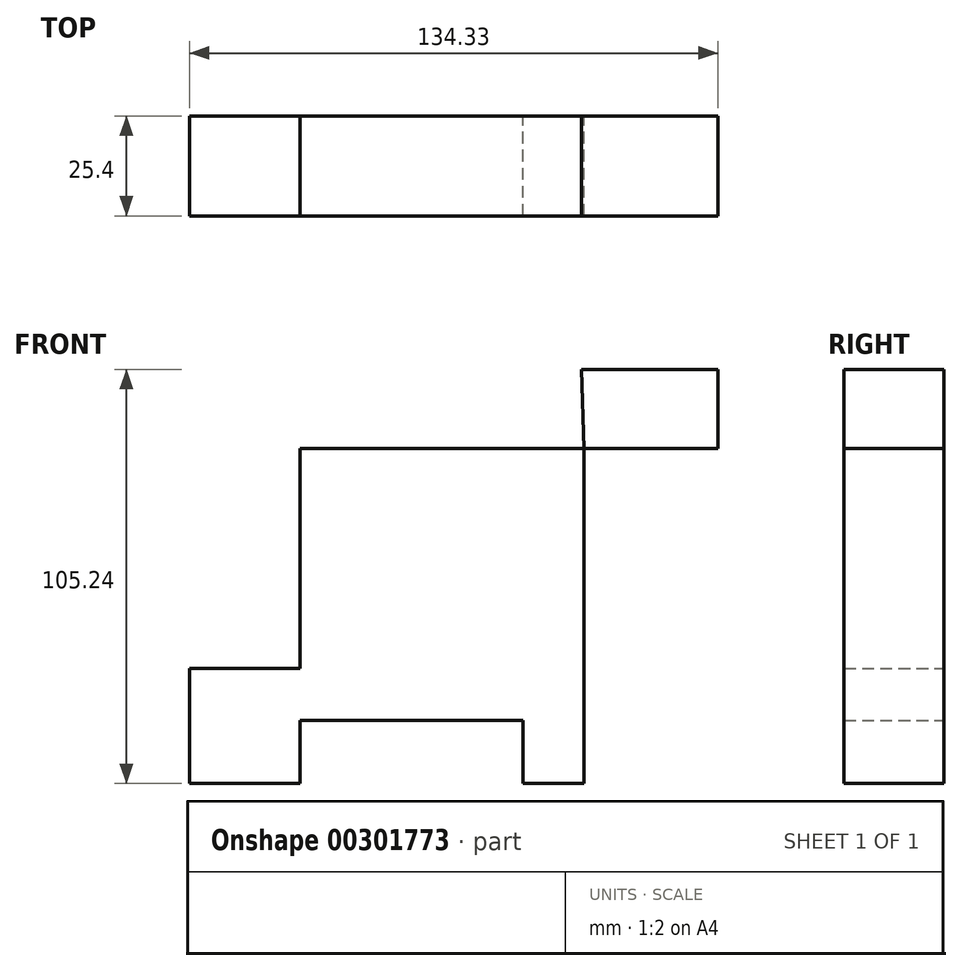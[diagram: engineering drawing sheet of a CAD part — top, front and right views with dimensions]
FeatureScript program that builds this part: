
annotation { "Feature Type Name" : "Feature", "Feature Type Description" : "" }
export const myFeature = defineFeature(function(context is Context, id is Id, definition is map)
    precondition{}
    {
        {
            var Q0;
            Q0=qCreatedBy(makeId("Front.planeOp"),FACE);
            var sketch = newSketch(context, id + "F0", { "sketchPlane" : qUnion([Q0])});
            skLineSegment(sketch, "E0", {"start": v(0, 55.87) * mm, "end": v(35.6, 55.87) * mm});
            skLineSegment(sketch, "E1", {"start": v(0, 55.87) * mm, "end": v(-36.52, 55.87) * mm});
            skLineSegment(sketch, "E2", {"start": v(-36.52, 55.87) * mm, "end": v(-36.52, 0) * mm});
            skLineSegment(sketch, "E3", {"start": v(-36.52, 0) * mm, "end": v(-64.69, 0) * mm});
            skLineSegment(sketch, "E4", {"start": v(-64.69, 0) * mm, "end": v(-64.69, -29.25) * mm});
            skLineSegment(sketch, "E5", {"start": v(-64.69, -29.25) * mm, "end": v(-36.52, -29.25) * mm});
            skLineSegment(sketch, "E6", {"start": v(-36.52, -29.25) * mm, "end": v(-36.52, -13.15) * mm});
            skLineSegment(sketch, "E7", {"start": v(35.6, 55.87) * mm, "end": v(35.6, -29.25) * mm});
            skLineSegment(sketch, "E8", {"start": v(35.6, -29.25) * mm, "end": v(20.12, -29.25) * mm});
            skLineSegment(sketch, "E9", {"start": v(20.12, -29.25) * mm, "end": v(20.12, -13.15) * mm});
            skLineSegment(sketch, "E10", {"start": v(-36.52, -13.15) * mm, "end": v(20.12, -13.15) * mm});
            skLineSegment(sketch, "E11", {"start": v(35.6, 55.87) * mm, "end": v(69.64, 55.87) * mm});
            skLineSegment(sketch, "E12", {"start": v(69.64, 55.87) * mm, "end": v(69.64, 75.99) * mm});
            skLineSegment(sketch, "E13", {"start": v(69.64, 75.99) * mm, "end": v(34.98, 75.99) * mm});
            skLineSegment(sketch, "E14", {"start": v(34.98, 75.99) * mm, "end": v(35.6, 55.87) * mm});
            skSolve(sketch);
        }
        {
            var Q0;
            Q0 = qSketchRegion(id + "F0", true);
            extrude(context, id + "F1", {"entities" : qUnion([Q0]), "depth" : 25.4 * mm});
        }
    });
